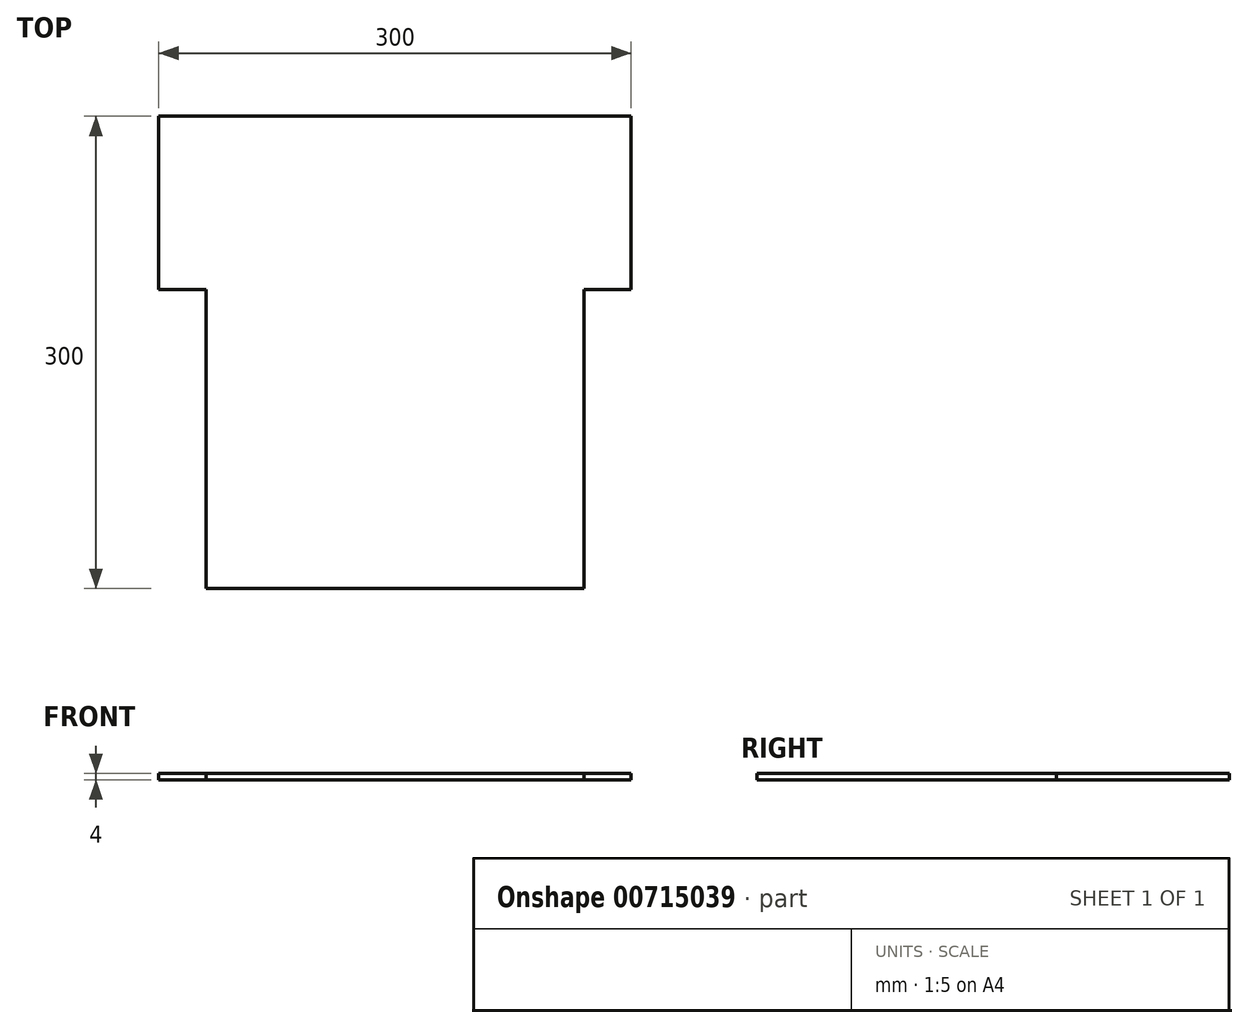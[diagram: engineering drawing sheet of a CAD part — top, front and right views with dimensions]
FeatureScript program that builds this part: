
annotation { "Feature Type Name" : "Feature", "Feature Type Description" : "" }
export const myFeature = defineFeature(function(context is Context, id is Id, definition is map)
    precondition{}
    {
        {
            var Q0;
            Q0=qCreatedBy(makeId("Top.planeOp"),FACE);
            var sketch = newSketch(context, id + "F0", { "sketchPlane" : qUnion([Q0])});
            skLineSegment(sketch, "E0.bottom", {"start": v(120, -150) * mm, "end": v(-120, -150) * mm});
            skLineSegment(sketch, "E0.top", {"start": v(150, 150) * mm, "end": v(-150, 150) * mm});
            skLineSegment(sketch, "E0.left", {"start": v(150, 40) * mm, "end": v(150, 150) * mm});
            skPoint(sketch, "E0.middle", {"position": v(0, 0) * mm});
            skLineSegment(sketch, "E1.top", {"start": v(-150, 40) * mm, "end": v(-120, 40) * mm});
            skLineSegment(sketch, "E1.right", {"start": v(-120, -150) * mm, "end": v(-120, 40) * mm});
            skLineSegment(sketch, "E2", {"start": v(-150, 40) * mm, "end": v(-150, 150) * mm});
            skPoint(sketch, "E3.end.orphan", {"position": v(-150, -150) * mm});
            skLineSegment(sketch, "E4.top", {"start": v(150, 40) * mm, "end": v(150, 40) * mm});
            skLineSegment(sketch, "E4.right", {"start": v(120, -150) * mm, "end": v(120, 40) * mm});
            skLineSegment(sketch, "E5", {"start": v(150, 40) * mm, "end": v(120, 40) * mm});
            skLineSegment(sketch, "E6", {"start": v(120, -150) * mm, "end": v(120, -150) * mm});
            skPoint(sketch, "E7.orphan", {"position": v(150, -150) * mm});
            skPoint(sketch, "E8", {"position": v(120, -55) * mm});
            skPoint(sketch, "E9", {"position": v(-120, -55) * mm});
            skSolve(sketch);
        }
        {
            var Q0;
            Q0=makeQuery(id+"F0.imprint","IMPRINT",FACE,{"disambiguationData":[TD([[makeQuery(id+"F0.imprint","IMPRINT",EDGE,{"derivedFrom":sQuery(id+"F0.wireOp",EDGE,"E0.bottom")}),-1.0]])]});
            extrude(context, id + "F1", {"entities" : qUnion([Q0]), "depth" : 4 * mm, "offsetDistance" : 25 * mm});
        }
    });
